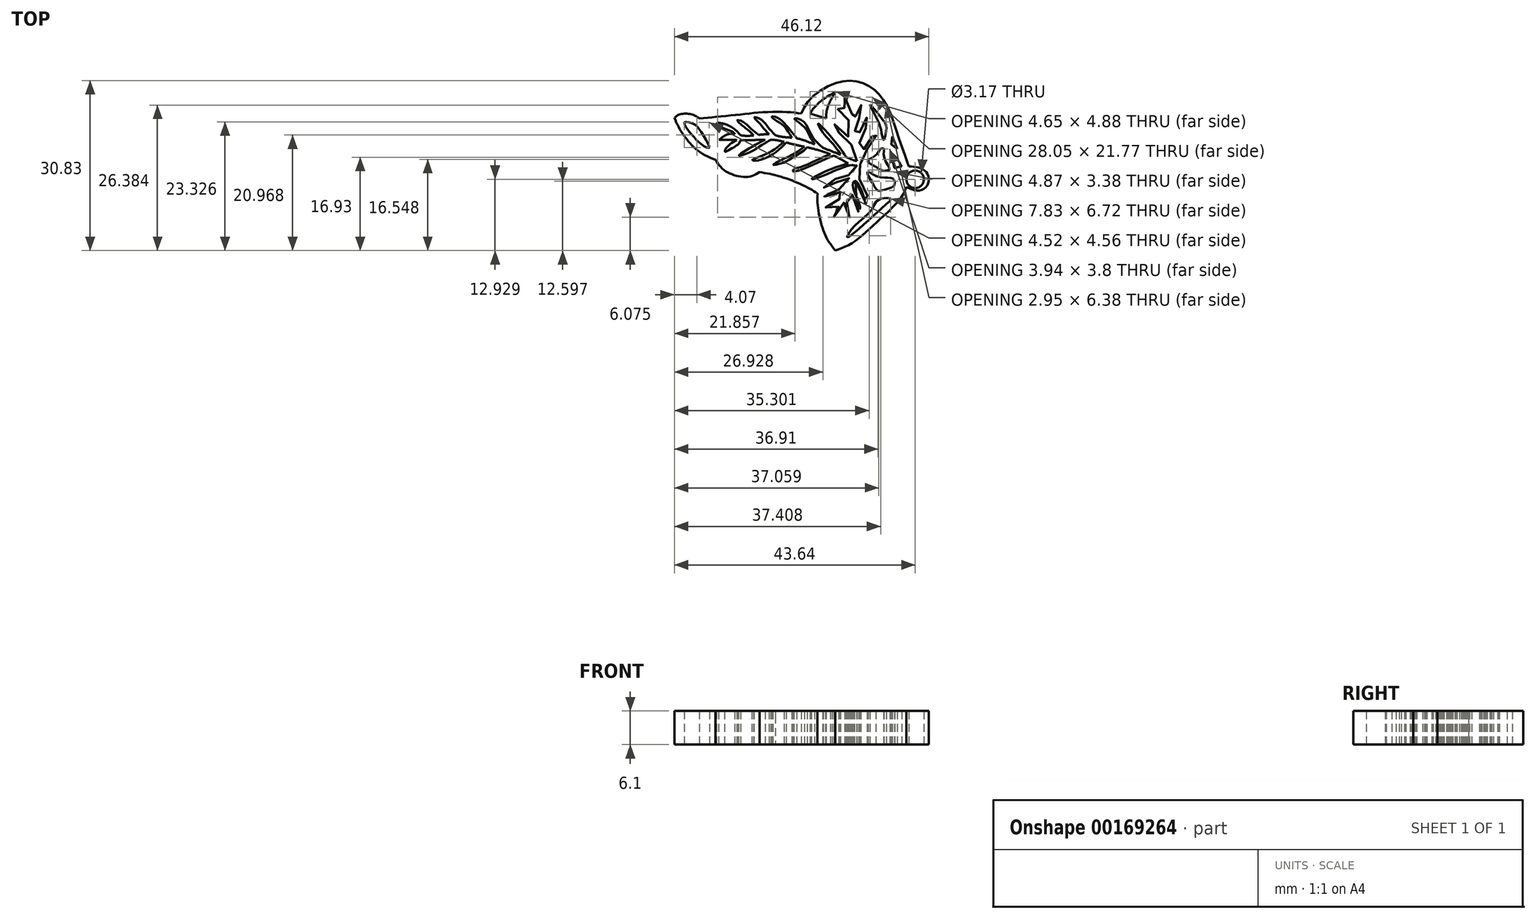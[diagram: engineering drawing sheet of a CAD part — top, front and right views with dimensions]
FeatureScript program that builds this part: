
annotation { "Feature Type Name" : "Feature", "Feature Type Description" : "" }
export const myFeature = defineFeature(function(context is Context, id is Id, definition is map)
    precondition{}
    {
        {
            var Q0;
            Q0=qCreatedBy(makeId("Top.planeOp"),FACE);
            var sketch = newSketch(context, id + "F0", { "sketchPlane" : qUnion([Q0])});
            skFitSpline(sketch, "E0", {"points": [v(-23.25, 8.52) * mm, v(-22.34, 9.14) * mm, v(-20.06, 9.14) * mm, v(-18.7, 8.4) * mm], "startDerivative": vector(2.65, 2.63) * mm, "endDerivative": vector(3.6, -2.65) * mm});
            skFitSpline(sketch, "E1", {"points": [v(-23.25, 8.52) * mm, v(-22.17, 6.3) * mm, v(-20.68, 4.25) * mm, v(-18.7, 2.38) * mm, v(-15.8, 0.9) * mm], "startDerivative": vector(3.96, -9.77) * mm, "endDerivative": vector(11.49, -4.62) * mm});
            skFitSpline(sketch, "E2", {"points": [v(-15.8, 0.9) * mm, v(-14.4, -0.8) * mm, v(-12.17, -1.92) * mm, v(-9.64, -2.12) * mm, v(-7.82, -1.31) * mm], "startDerivative": vector(5.09, -7.52) * mm, "endDerivative": vector(7.35, 4.37) * mm});
            skFitSpline(sketch, "E3", {"points": [v(-7.82, -1.31) * mm, v(-5.14, -1.82) * mm, v(-1.95, -2.83) * mm, v(0.99, -4.15) * mm, v(2.71, -5.21) * mm], "startDerivative": vector(10.68, -1.71) * mm, "endDerivative": vector(7.48, -4.98) * mm});
            skFitSpline(sketch, "E4", {"points": [v(2.71, -5.21) * mm, v(2.71, -7.24) * mm, v(3.37, -10.63) * mm, v(4.38, -13.36) * mm, v(5.9, -15.54) * mm], "startDerivative": vector(-0.49, -8.8) * mm, "endDerivative": vector(6.47, -9.45) * mm});
            skFitSpline(sketch, "E5", {"points": [v(5.9, -15.54) * mm, v(9.04, -14.13) * mm, v(13.3, -10.53) * mm, v(17.75, -6.08) * mm, v(18.81, -4) * mm], "startDerivative": vector(13.9, 5.01) * mm, "endDerivative": vector(3.93, 10.49) * mm});
            skFitSpline(sketch, "E6", {"points": [v(18.81, -4) * mm, v(21.25, -4.65) * mm, v(22.7, -3.5) * mm, v(22.6, -1.62) * mm, v(21.24, -0.55) * mm, v(19.22, -0.26) * mm], "startDerivative": vector(11.22, -5.42) * mm, "endDerivative": vector(-10.45, 0.6) * mm});
            skFitSpline(sketch, "E7", {"points": [v(19.22, -0.26) * mm, v(18.7, 1.4) * mm, v(17.22, 5.43) * mm, v(15.85, 9.6) * mm, v(14.18, 12.37) * mm, v(12.6, 13.96) * mm, v(10.03, 15.1) * mm, v(7.66, 15.21) * mm, v(4.25, 14.08) * mm, v(1.14, 11.68) * mm, v(-0.26, 9.3) * mm], "startDerivative": vector(-5.64, 19.64) * mm, "endDerivative": vector(-11.57, -26.36) * mm});
            skFitSpline(sketch, "E8", {"points": [v(-18.7, 8.4) * mm, v(-15.22, 8.75) * mm, v(-10.81, 9.2) * mm, v(-6.98, 9.56) * mm, v(-2.66, 9.58) * mm, v(-0.26, 9.3) * mm], "startDerivative": vector(17.1, 1.72) * mm, "endDerivative": vector(13.47, -2.07) * mm});
            skFitSpline(sketch, "E9", {"points": [v(6, 13.29) * mm, v(3.64, 11.82) * mm, v(1.96, 10.24) * mm, v(1.35, 9.3) * mm], "startDerivative": vector(-6.2, -3.5) * mm, "endDerivative": vector(-2, -3.61) * mm});
            skFitSpline(sketch, "E10", {"points": [v(6, 13.29) * mm, v(5.15, 11.85) * mm, v(4.4, 10) * mm, v(4.25, 8.4) * mm], "startDerivative": vector(-2.67, -4.18) * mm, "endDerivative": vector(-0.07, -4.89) * mm});
            skLineSegment(sketch, "E11", {"start": v(1.35, 9.3) * mm, "end": v(4.25, 8.4) * mm});
            skFitSpline(sketch, "E12", {"points": [v(12.18, 10.98) * mm, v(14.61, 8.08) * mm, v(15.16, 6.72) * mm, v(14.7, 4.55) * mm, v(14.4, 5.36) * mm, v(13.67, 7.96) * mm, v(12.18, 10.98) * mm]});
            skFitSpline(sketch, "E13", {"points": [v(14.12, 2.9) * mm, v(13.4, 1.85) * mm, v(11.98, 0.92) * mm, v(11.86, 0.47) * mm, v(13.1, -0.22) * mm, v(14.15, -0.89) * mm, v(15.75, -0.89) * mm, v(15.17, 0.4) * mm, v(14.7, 2.27) * mm, v(14.7, 2.97) * mm, v(14.12, 2.9) * mm]});
            skLineSegment(sketch, "E14", {"start": v(16.26, 5.16) * mm, "end": v(16.05, 3.74) * mm});
            skLineSegment(sketch, "E15", {"start": v(16.05, 3.74) * mm, "end": v(17.17, 2.9) * mm});
            skLineSegment(sketch, "E16", {"start": v(17.17, 2.9) * mm, "end": v(16.26, 5.16) * mm});
            skFitSpline(sketch, "E17", {"points": [v(16.13, 2.1) * mm, v(16.37, 0.56) * mm, v(16.65, -0.58) * mm], "startDerivative": vector(0.41, -2.97) * mm, "endDerivative": vector(0.64, -2.36) * mm});
            skFitSpline(sketch, "E18", {"points": [v(16.13, 2.1) * mm, v(17, 1.27) * mm, v(17.96, -0.28) * mm], "startDerivative": vector(1.97, -1.63) * mm, "endDerivative": vector(1.7, -3.06) * mm});
            skFitSpline(sketch, "E19", {"points": [v(16.65, -0.58) * mm, v(17.26, -0.41) * mm, v(17.96, -0.28) * mm], "startDerivative": vector(1.23, 0.38) * mm, "endDerivative": vector(1.38, 0.23) * mm});
            skCircle(sketch, "E20", {"center": v(20.4, -2.61) * mm, "radius": 1.59 * mm});
            skFitSpline(sketch, "E21", {"points": [v(11.72, -1.25) * mm, v(13.57, -2.12) * mm, v(15.84, -2.34) * mm, v(16.63, -2.75) * mm, v(16.5, -3.8) * mm, v(14.88, -4.48) * mm, v(13.76, -4.73) * mm, v(12.87, -3.68) * mm, v(11.72, -1.25) * mm]});
            skFitSpline(sketch, "E22", {"points": [v(15.97, -6.1) * mm, v(13.67, -6.36) * mm, v(12.68, -7.92) * mm, v(10.38, -10.15) * mm, v(8.57, -12.1) * mm, v(8.09, -13.15) * mm, v(10.38, -11.43) * mm, v(12.78, -9.3) * mm, v(15.26, -7.03) * mm, v(15.97, -6.1) * mm]});
            skFitSpline(sketch, "E23", {"points": [v(-21.44, 7.7) * mm, v(-19.8, 7.42) * mm, v(-18.47, 6.06) * mm, v(-16.93, 3.13) * mm, v(-18.22, 3.63) * mm, v(-20.08, 5.49) * mm, v(-21.44, 7.7) * mm]});
            skFitSpline(sketch, "E24", {"points": [v(9.27, 0.81) * mm, v(6.25, 2.1) * mm, v(2.16, 3.7) * mm, v(-1.07, 4.82) * mm, v(-3.88, 5.11) * mm, v(-5.84, 5.54) * mm, v(-8.56, 5.37) * mm, v(-10.95, 5.33) * mm, v(-13.42, 5.58) * mm, v(-15.16, 4.52) * mm], "startDerivative": vector(-23.84, 10.32) * mm, "endDerivative": vector(-16.97, -14.84) * mm});
            skFitSpline(sketch, "E25", {"points": [v(-15.16, 4.52) * mm, v(-12.44, 4.52) * mm, v(-8.44, 4.52) * mm, v(-5.03, 4.52) * mm, v(-2.1, 3.84) * mm, v(1.18, 3.11) * mm, v(5.91, 1.54) * mm, v(8.93, 0) * mm, v(10.25, 0) * mm, v(10.55, 0.39) * mm, v(9.27, 0.81) * mm], "startDerivative": vector(25.15, 0.12) * mm, "endDerivative": vector(-25.08, 4.53) * mm});
            skFitSpline(sketch, "E26", {"points": [v(10.55, 0.39) * mm, v(11.17, 2.34) * mm, v(12.45, 3.56) * mm, v(13.34, 5.6) * mm, v(12.86, 6.01) * mm, v(12.58, 5.05) * mm, v(11.9, 3.59) * mm, v(10.55, 2.6) * mm, v(10.25, 3.14) * mm, v(10.55, 4.96) * mm, v(11.56, 6.97) * mm, v(11.88, 8.66) * mm, v(11.46, 8.44) * mm, v(10.55, 6.36) * mm, v(9.87, 5.18) * mm, v(9.55, 5.79) * mm, v(9.58, 7.35) * mm, v(10.25, 8.53) * mm, v(10.55, 10.32) * mm, v(10.55, 10.9) * mm, v(9.87, 9.62) * mm, v(9.27, 8.28) * mm, v(8.97, 8.28) * mm, v(8.97, 10) * mm, v(7.44, 12.36) * mm, v(6.77, 12.17) * mm, v(7.76, 11.27) * mm, v(8.14, 9.97) * mm, v(6.9, 10.67) * mm, v(5.95, 10.46) * mm, v(7.73, 9.42) * mm, v(8.4, 7.67) * mm, v(8.37, 5.12) * mm, v(6.45, 7.1) * mm, v(5.4, 7.26) * mm, v(6.2, 6.2) * mm, v(8.2, 4.26) * mm, v(9.27, 2.98) * mm, v(9.87, 0.39) * mm, v(9.87, -0.11) * mm], "startDerivative": vector(13.71, 71.53) * mm, "endDerivative": vector(-2.05, -24.55) * mm});
            skFitSpline(sketch, "E27", {"points": [v(7.93, 1.4) * mm, v(5.85, 4.3) * mm, v(2.79, 7.47) * mm, v(3.45, 6.17) * mm, v(4.56, 4.82) * mm, v(6.83, 1.85) * mm], "startDerivative": vector(-7.86, 11.47) * mm, "endDerivative": vector(6.4, -14.78) * mm});
            skFitSpline(sketch, "E28", {"points": [v(3.6, 3.14) * mm, v(2.16, 4.6) * mm, v(1.14, 6.3) * mm, v(0, 7.97) * mm, v(-1.49, 8.43) * mm, v(-1.1, 7.97) * mm, v(0.28, 6.87) * mm, v(1.3, 5.25) * mm, v(2.16, 3.7) * mm], "startDerivative": vector(-10.95, 10.24) * mm, "endDerivative": vector(6.69, -11.7) * mm});
            skFitSpline(sketch, "E29", {"points": [v(-1.07, 4.82) * mm, v(-2.02, 6.06) * mm, v(-3.28, 7.52) * mm, v(-4.79, 8.67) * mm, v(-5.6, 8.74) * mm, v(-4.95, 8.14) * mm, v(-3.5, 7.14) * mm, v(-1.95, 4.93) * mm], "startDerivative": vector(-6.39, 8.66) * mm, "endDerivative": vector(7.88, -13.54) * mm});
            skFitSpline(sketch, "E30", {"points": [v(-4.97, 5.38) * mm, v(-6.39, 6.97) * mm, v(-7.51, 8.21) * mm, v(-8.75, 8.64) * mm, v(-8.27, 7.99) * mm, v(-7.96, 7.69) * mm, v(-6.65, 6.16) * mm, v(-6.1, 5.56) * mm], "startDerivative": vector(-8.13, 8.87) * mm, "endDerivative": vector(4.3, -4.58) * mm});
            skFitSpline(sketch, "E31", {"points": [v(-7.96, 5.44) * mm, v(-9.47, 6.63) * mm, v(-10.57, 7.66) * mm, v(-11.83, 8.12) * mm, v(-11.06, 7.25) * mm, v(-10.54, 6.85) * mm, v(-8.9, 5.33) * mm], "startDerivative": vector(-8.54, 6.26) * mm, "endDerivative": vector(6.99, -8.28) * mm});
            skFitSpline(sketch, "E32", {"points": [v(-11.24, 5.37) * mm, v(-12.86, 6.85) * mm, v(-14.58, 7.54) * mm, v(-15.54, 7.64) * mm, v(-15.28, 7.14) * mm, v(-12.8, 6.04) * mm, v(-12.28, 5.56) * mm], "startDerivative": vector(-7.44, 7.85) * mm, "endDerivative": vector(2.6, -4.12) * mm});
            skFitSpline(sketch, "E33", {"points": [v(-11.92, 4.51) * mm, v(-13.6, 3.38) * mm, v(-14.08, 2.42) * mm, v(-13.17, 2.82) * mm, v(-11.72, 3.7) * mm, v(-11.24, 4.5) * mm], "startDerivative": vector(-7.37, -3.75) * mm, "endDerivative": vector(2.09, 4.97) * mm});
            skFitSpline(sketch, "E34", {"points": [v(-6.81, 4.58) * mm, v(-8.43, 3.7) * mm, v(-10.84, 2.29) * mm, v(-11.57, 1.7) * mm, v(-9.83, 2.19) * mm, v(-7.22, 3.7) * mm, v(-5.79, 4.58) * mm], "startDerivative": vector(-9.33, -4.86) * mm, "endDerivative": vector(8.81, 4.51) * mm});
            skFitSpline(sketch, "E35", {"points": [v(-3.38, 4.18) * mm, v(-4.89, 3) * mm, v(-7.17, 1.73) * mm, v(-9.12, 0.87) * mm, v(-7.98, 0.82) * mm, v(-4.89, 2.29) * mm, v(-2.96, 4.07) * mm], "startDerivative": vector(-9.44, -7.77) * mm, "endDerivative": vector(9.57, 10) * mm});
            skFitSpline(sketch, "E36", {"points": [v(0.34, 3.3) * mm, v(-0.98, 2.37) * mm, v(-3.28, 1.16) * mm, v(-5.32, 0) * mm, v(-3.66, 0.33) * mm, v(-3.25, 0.5) * mm, v(-0.28, 2.26) * mm, v(0.84, 3.2) * mm], "startDerivative": vector(-9.23, -6.88) * mm, "endDerivative": vector(7.54, 6.88) * mm});
            skFitSpline(sketch, "E37", {"points": [v(5.03, 1.93) * mm, v(2.62, 0.89) * mm, v(-0.22, -0.34) * mm, v(-1.57, -0.78) * mm, v(-1.75, -1.17) * mm, v(0.74, -0.45) * mm, v(4.23, 1.1) * mm, v(5.64, 1.66) * mm], "startDerivative": vector(-14.28, -5.57) * mm, "endDerivative": vector(10.25, 3.35) * mm});
            skFitSpline(sketch, "E38", {"points": [v(8.26, 0.28) * mm, v(5.08, -0.78) * mm, v(2.44, -2) * mm, v(1.65, -2.52) * mm, v(2.01, -2.55) * mm, v(4.6, -1.6) * mm, v(7.61, -0.35) * mm, v(8.93, 0) * mm], "startDerivative": vector(-17.16, -5.29) * mm, "endDerivative": vector(9.97, 2.2) * mm});
            skFitSpline(sketch, "E39", {"points": [v(9.87, -0.11) * mm, v(9.45, -1.33) * mm, v(7.84, -1.96) * mm, v(6.57, -2.32) * mm, v(5.17, -2.96) * mm, v(3.93, -3.91) * mm, v(3.91, -4.37) * mm, v(6.1, -3.17) * mm, v(7.93, -2.41) * mm, v(8.39, -2.4) * mm, v(8.14, -3.38) * mm, v(6.02, -4.65) * mm, v(4.18, -5.4) * mm, v(3.86, -6.2) * mm, v(7.56, -4.8) * mm, v(7.27, -5.75) * mm, v(5.7, -6.64) * mm, v(4.2, -7.72) * mm, v(6.42, -7.14) * mm, v(6.2, -8.33) * mm, v(5.4, -9.43) * mm, v(6.82, -8.79) * mm, v(7.52, -6.76) * mm, v(8.18, -8.88) * mm, v(8.66, -9.66) * mm, v(7.93, -5.98) * mm, v(8.56, -4.97) * mm, v(9.62, -7) * mm, v(10.1, -8.5) * mm, v(10.38, -7.53) * mm, v(9.13, -4.06) * mm, v(9.49, -2.89) * mm, v(10.95, -5.4) * mm, v(11.5, -7.15) * mm, v(11.75, -5.75) * mm, v(10.46, -3.15) * mm, v(10.3, -1.5) * mm, v(10.45, 0.13) * mm], "startDerivative": vector(-7.2, -58.48) * mm, "endDerivative": vector(5.5, 62.18) * mm});
            skLineSegment(sketch, "E40", {"start": v(-6.1, 5.56) * mm, "end": v(-6.1, 5.56) * mm});
            skLineSegment(sketch, "E41", {"start": v(-4.97, 5.38) * mm, "end": v(-4.88, 5.35) * mm});
            skSolve(sketch);
        }
        {
            var Q0;
            Q0=makeQuery(id+"F0.imprint","IMPRINT",FACE,{"disambiguationData":[TD([[makeQuery(id+"F0.imprint","IMPRINT",EDGE,{"derivedFrom":sQuery(id+"F0.wireOp",EDGE,"E3")}),1.0]])]});
            var Q1;
            Q1=makeQuery(id+"F0.imprint","IMPRINT",FACE,{"disambiguationData":[TD([[makeQuery(id+"F0.imprint","IMPRINT",EDGE,{"derivedFrom":sQuery(id+"F0.wireOp",EDGE,"E1")}),1.0]])]});
            extrude(context, id + "F1", {"entities" : qUnion([Q0, Q1]), "depth" : 5.33 * mm});
        }
        {
            var Q0;
            Q0=makeQuery(id+"F0.imprint","IMPRINT",FACE,{"disambiguationData":[TD([[makeQuery(id+"F0.imprint","IMPRINT",EDGE,{"derivedFrom":sQuery(id+"F0.wireOp",EDGE,"E0")}),-1.0]])]});
            extrude(context, id + "F2", {"entities" : qUnion([Q0]), "operationType" : NewBodyOperationType.ADD, "depth" : 6.1 * mm});
        }
        {
            var Q0;
            Q0=makeQuery(id+"F0.imprint","IMPRINT",FACE,{"disambiguationData":[TD([[makeQuery(id+"F0.imprint","IMPRINT",EDGE,{"derivedFrom":sQuery(id+"F0.wireOp",EDGE,"E6")}),1.0]])]});
            extrude(context, id + "F3", {"entities" : qUnion([Q0]), "operationType" : NewBodyOperationType.ADD, "depth" : 3.17 * mm});
        }
    });
